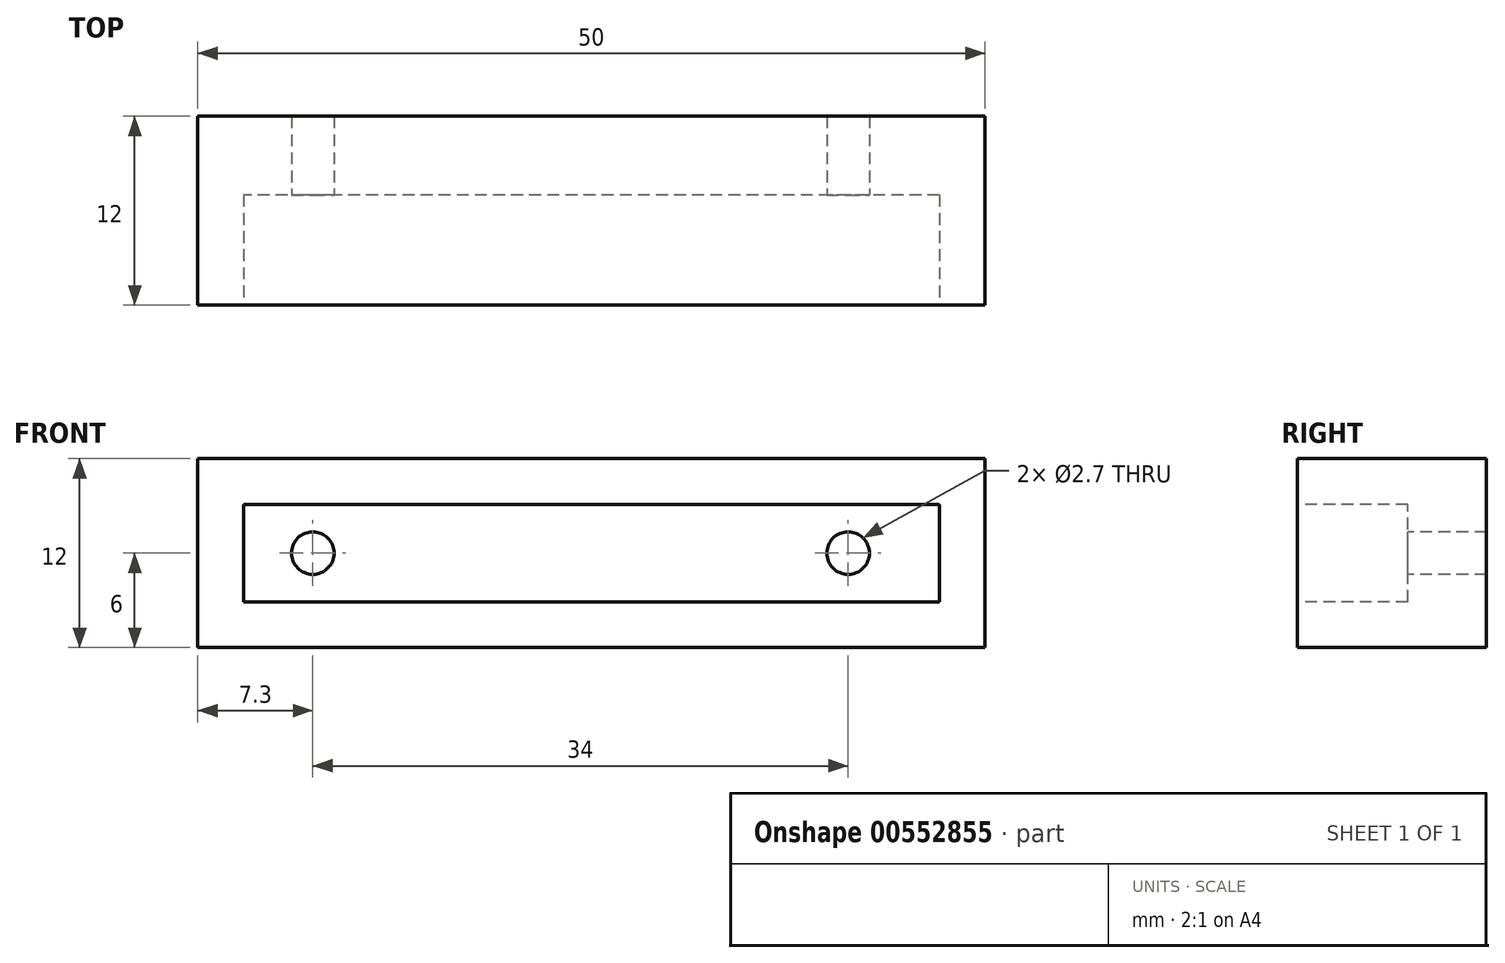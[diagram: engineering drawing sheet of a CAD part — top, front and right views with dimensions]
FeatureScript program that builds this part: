
annotation { "Feature Type Name" : "Feature", "Feature Type Description" : "" }
export const myFeature = defineFeature(function(context is Context, id is Id, definition is map)
    precondition{}
    {
        {
            var Q0;
            Q0=qCreatedBy(makeId("Front.planeOp"),FACE);
            var sketch = newSketch(context, id + "F0", { "sketchPlane" : qUnion([Q0])});
            skLineSegment(sketch, "E0.bottom", {"start": v(25, -6) * mm, "end": v(-25, -6) * mm});
            skLineSegment(sketch, "E0.top", {"start": v(25, 6) * mm, "end": v(-25, 6) * mm});
            skLineSegment(sketch, "E0.left", {"start": v(25, -6) * mm, "end": v(25, 6) * mm});
            skLineSegment(sketch, "E0.right", {"start": v(-25, -6) * mm, "end": v(-25, 6) * mm});
            skPoint(sketch, "E0.middle", {"position": v(0, 0) * mm});
            skSolve(sketch);
        }
        {
            var Q0;
            Q0=makeQuery(id+"F0.imprint","IMPRINT",FACE,{"disambiguationData":[TD([[makeQuery(id+"F0.imprint","IMPRINT",EDGE,{"derivedFrom":sQuery(id+"F0.wireOp",EDGE,"E0.bottom")}),-1.0]])]});
            extrude(context, id + "F1", {"entities" : qUnion([Q0]), "depth" : 12 * mm, "offsetDistance" : 25 * mm});
        }
        {
            var Q0;
            Q0=makeQuery(id+"F1.opExtrude","CAP_FACE",FACE,{"disambiguationData":[OSD([sQuery(id+"F0.wireOp",EDGE,"E0.bottom"),sQuery(id+"F0.wireOp",EDGE,"E0.top"),sQuery(id+"F0.wireOp",EDGE,"E0.left"),sQuery(id+"F0.wireOp",EDGE,"E0.right")])],"isStart":false});
            var sketch = newSketch(context, id + "F2", { "sketchPlane" : qUnion([Q0])});
            skLineSegment(sketch, "E1.bottom", {"start": v(22.1, -3.1) * mm, "end": v(-22.1, -3.1) * mm});
            skLineSegment(sketch, "E1.top", {"start": v(22.1, 3.1) * mm, "end": v(-22.1, 3.1) * mm});
            skLineSegment(sketch, "E1.left", {"start": v(22.1, -3.1) * mm, "end": v(22.1, 3.1) * mm});
            skLineSegment(sketch, "E1.right", {"start": v(-22.1, -3.1) * mm, "end": v(-22.1, 3.1) * mm});
            skPoint(sketch, "E1.middle", {"position": v(0, 0) * mm});
            skSolve(sketch);
        }
        {
            var Q0;
            Q0=makeQuery(id+"F2.imprint","IMPRINT",FACE,{"disambiguationData":[TD([[makeQuery(id+"F2.imprint","IMPRINT",EDGE,{"derivedFrom":sQuery(id+"F2.wireOp",EDGE,"E1.bottom")}),-1.0]])]});
            extrude(context, id + "F3", {"entities" : qUnion([Q0]), "operationType" : NewBodyOperationType.REMOVE, "oppositeDirection" : true, "depth" : 7 * mm, "offsetDistance" : 25 * mm});
        }
        {
            var Q0;
            Q0=makeQuery(id+"F3.boolean.opBoolean","COPY",FACE,{"derivedFrom":makeQuery(id+"F3.opExtrude","CAP_FACE",FACE,{"disambiguationData":[OSD([sQuery(id+"F2.wireOp",EDGE,"E1.bottom"),sQuery(id+"F2.wireOp",EDGE,"E1.top"),sQuery(id+"F2.wireOp",EDGE,"E1.left"),sQuery(id+"F2.wireOp",EDGE,"E1.right")])],"isStart":false})});
            var sketch = newSketch(context, id + "F4", { "sketchPlane" : qUnion([Q0])});
            skCircle(sketch, "E2", {"center": v(-17.7, 0) * mm, "radius": 1.35 * mm});
            skCircle(sketch, "E3", {"center": v(16.3, 0) * mm, "radius": 1.35 * mm});
            skSolve(sketch);
        }
        {
            var Q0;
            Q0=makeQuery(id+"F4.imprint","IMPRINT",FACE,{"disambiguationData":[TD([[makeQuery(id+"F4.imprint","IMPRINT",EDGE,{"derivedFrom":sQuery(id+"F4.wireOp",EDGE,"E2")}),1.0]])]});
            var Q1;
            Q1=makeQuery(id+"F4.imprint","IMPRINT",FACE,{"disambiguationData":[TD([[makeQuery(id+"F4.imprint","IMPRINT",EDGE,{"derivedFrom":sQuery(id+"F4.wireOp",EDGE,"E3")}),1.0]])]});
            extrude(context, id + "F5", {"entities" : qUnion([Q0, Q1]), "operationType" : NewBodyOperationType.REMOVE, "endBound" : BoundingType.UP_TO_NEXT, "oppositeDirection" : true, "depth" : 25 * mm, "offsetDistance" : 25 * mm});
        }
    });
